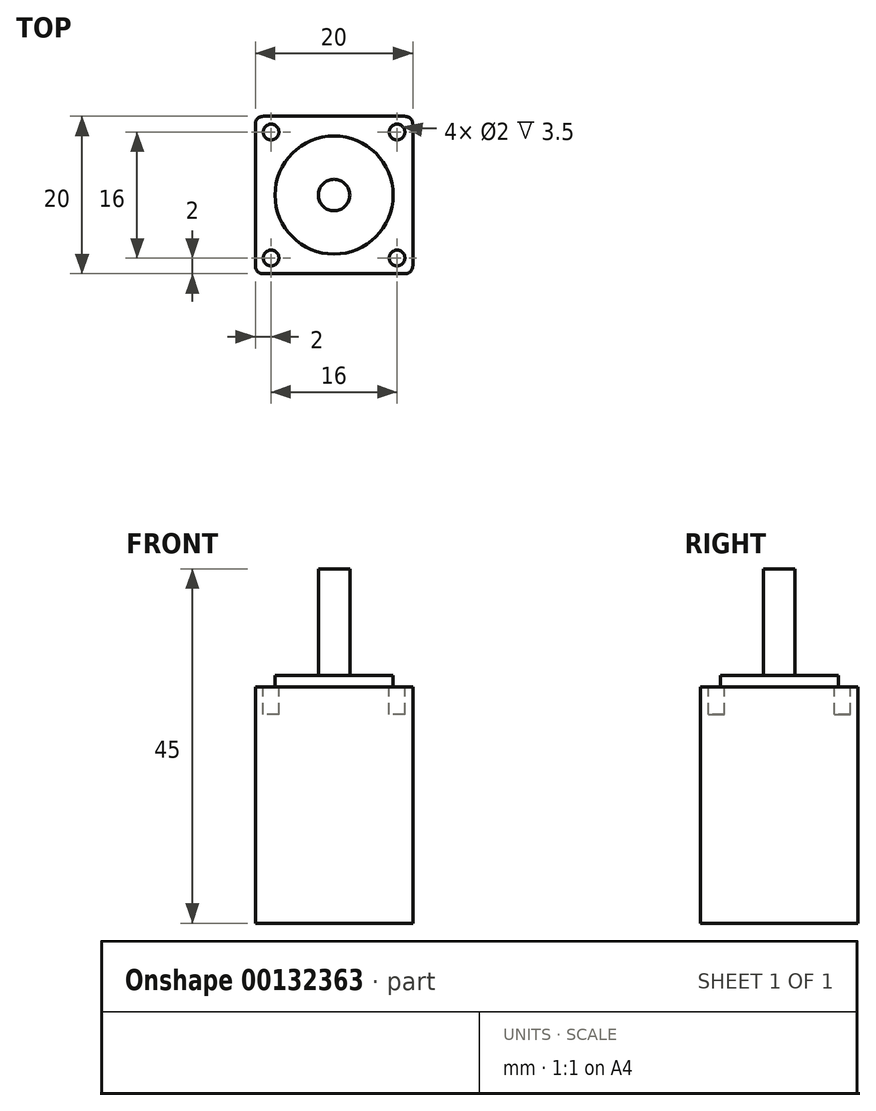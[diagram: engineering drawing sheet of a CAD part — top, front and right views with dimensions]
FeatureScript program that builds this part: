
annotation { "Feature Type Name" : "Feature", "Feature Type Description" : "" }
export const myFeature = defineFeature(function(context is Context, id is Id, definition is map)
    precondition{}
    {
        {
            var Q0;
            Q0=qCreatedBy(makeId("Top.planeOp"),FACE);
            var sketch = newSketch(context, id + "F0", { "sketchPlane" : qUnion([Q0])});
            skPoint(sketch, "E0.middle", {"position": v(0, 0) * mm});
            skLineSegment(sketch, "E1.bottom", {"start": v(9, 10) * mm, "end": v(-9, 10) * mm});
            skLineSegment(sketch, "E1.top", {"start": v(9, -10) * mm, "end": v(-9, -10) * mm});
            skLineSegment(sketch, "E1.left", {"start": v(10, 9) * mm, "end": v(10, -9) * mm});
            skLineSegment(sketch, "E1.right", {"start": v(-10, 9) * mm, "end": v(-10, -9) * mm});
            skCircle(sketch, "E2", {"center": v(-8, -8) * mm, "radius": 1 * mm});
            skCircle(sketch, "E3.0.1.0", {"center": v(-8, 8) * mm, "radius": 1 * mm});
            skCircle(sketch, "E3.1.0.0", {"center": v(8, -8) * mm, "radius": 1 * mm});
            skCircle(sketch, "E3.1.1.0", {"center": v(8, 8) * mm, "radius": 1 * mm});
            skLineSegment(sketch, "E3.direction1", {"start": v(-8, -8) * mm, "end": v(8, -8) * mm, "construction": true});
            skLineSegment(sketch, "E3.direction2", {"start": v(-8, -8) * mm, "end": v(-8, 8) * mm, "construction": true});
            skCircle(sketch, "E4", {"center": v(0, 0) * mm, "radius": 7.5 * mm});
            skCircle(sketch, "E5", {"center": v(0, 0) * mm, "radius": 2 * mm});
            skPoint(sketch, "E6.visualSharp", {"position": v(-10, -10) * mm});
            skArc(sketch, "E6.filletArc", {"start": v(-10, -9) * mm, "mid": v(-9.7, -9.7) * mm, "end": v(-9, -10) * mm});
            skPoint(sketch, "E7.visualSharp", {"position": v(-10, 10) * mm});
            skArc(sketch, "E7.filletArc", {"start": v(-9, 10) * mm, "mid": v(-9.7, 9.7) * mm, "end": v(-10, 9) * mm});
            skPoint(sketch, "E8.visualSharp", {"position": v(10, 10) * mm});
            skArc(sketch, "E8.filletArc", {"start": v(10, 9) * mm, "mid": v(9.7, 9.7) * mm, "end": v(9, 10) * mm});
            skPoint(sketch, "E9.visualSharp", {"position": v(10, -10) * mm});
            skArc(sketch, "E9.filletArc", {"start": v(9, -10) * mm, "mid": v(9.7, -9.7) * mm, "end": v(10, -9) * mm});
            skSolve(sketch);
        }
        {
            var Q0;
            Q0=makeQuery(id+"F0.imprint","IMPRINT",FACE,{"disambiguationData":[TD([[makeQuery(id+"F0.imprint","IMPRINT",EDGE,{"derivedFrom":sQuery(id+"F0.wireOp",EDGE,"E4")}),1.0]])]});
            var Q1;
            Q1=makeQuery(id+"F0.imprint","IMPRINT",FACE,{"disambiguationData":[TD([[makeQuery(id+"F0.imprint","IMPRINT",EDGE,{"derivedFrom":sQuery(id+"F0.wireOp",EDGE,"E2")}),1.0]])]});
            var Q2;
            Q2=makeQuery(id+"F0.imprint","IMPRINT",FACE,{"disambiguationData":[TD([[makeQuery(id+"F0.imprint","IMPRINT",EDGE,{"derivedFrom":sQuery(id+"F0.wireOp",EDGE,"E1.bottom")}),1.0]])]});
            var Q3;
            Q3=makeQuery(id+"F0.imprint","IMPRINT",FACE,{"disambiguationData":[TD([[makeQuery(id+"F0.imprint","IMPRINT",EDGE,{"derivedFrom":sQuery(id+"F0.wireOp",EDGE,"E5")}),1.0]])]});
            var Q4;
            Q4=makeQuery(id+"F0.imprint","IMPRINT",FACE,{"disambiguationData":[TD([[makeQuery(id+"F0.imprint","IMPRINT",EDGE,{"derivedFrom":sQuery(id+"F0.wireOp",EDGE,"E3.1.1.0")}),1.0]])]});
            var Q5;
            Q5=makeQuery(id+"F0.imprint","IMPRINT",FACE,{"disambiguationData":[TD([[makeQuery(id+"F0.imprint","IMPRINT",EDGE,{"derivedFrom":sQuery(id+"F0.wireOp",EDGE,"E3.1.0.0")}),1.0]])]});
            var Q6;
            Q6=makeQuery(id+"F0.imprint","IMPRINT",FACE,{"disambiguationData":[TD([[makeQuery(id+"F0.imprint","IMPRINT",EDGE,{"derivedFrom":sQuery(id+"F0.wireOp",EDGE,"E3.0.1.0")}),1.0]])]});
            extrude(context, id + "F1", {"entities" : qUnion([Q0, Q1, Q2, Q3, Q4, Q5, Q6]), "oppositeDirection" : true, "depth" : 30 * mm});
        }
        {
            var Q0;
            Q0=makeQuery(id+"F0.imprint","IMPRINT",FACE,{"disambiguationData":[TD([[makeQuery(id+"F0.imprint","IMPRINT",EDGE,{"derivedFrom":sQuery(id+"F0.wireOp",EDGE,"E3.0.1.0")}),1.0]])]});
            var Q1;
            Q1=makeQuery(id+"F0.imprint","IMPRINT",FACE,{"disambiguationData":[TD([[makeQuery(id+"F0.imprint","IMPRINT",EDGE,{"derivedFrom":sQuery(id+"F0.wireOp",EDGE,"E3.1.1.0")}),1.0]])]});
            var Q2;
            Q2=makeQuery(id+"F0.imprint","IMPRINT",FACE,{"disambiguationData":[TD([[makeQuery(id+"F0.imprint","IMPRINT",EDGE,{"derivedFrom":sQuery(id+"F0.wireOp",EDGE,"E2")}),1.0]])]});
            var Q3;
            Q3=makeQuery(id+"F0.imprint","IMPRINT",FACE,{"disambiguationData":[TD([[makeQuery(id+"F0.imprint","IMPRINT",EDGE,{"derivedFrom":sQuery(id+"F0.wireOp",EDGE,"E3.1.0.0")}),1.0]])]});
            extrude(context, id + "F2", {"entities" : qUnion([Q0, Q1, Q2, Q3]), "operationType" : NewBodyOperationType.REMOVE, "oppositeDirection" : true, "depth" : 3.5 * mm});
        }
        {
            var Q0;
            Q0=makeQuery(id+"F0.imprint","IMPRINT",FACE,{"disambiguationData":[TD([[makeQuery(id+"F0.imprint","IMPRINT",EDGE,{"derivedFrom":sQuery(id+"F0.wireOp",EDGE,"E5")}),1.0]])]});
            extrude(context, id + "F3", {"entities" : qUnion([Q0]), "operationType" : NewBodyOperationType.ADD, "depth" : 15 * mm});
        }
        {
            var Q0;
            Q0=makeQuery(id+"F0.imprint","IMPRINT",FACE,{"disambiguationData":[TD([[makeQuery(id+"F0.imprint","IMPRINT",EDGE,{"derivedFrom":sQuery(id+"F0.wireOp",EDGE,"E4")}),1.0]])]});
            extrude(context, id + "F4", {"entities" : qUnion([Q0]), "operationType" : NewBodyOperationType.ADD, "depth" : 1.5 * mm});
        }
    });
